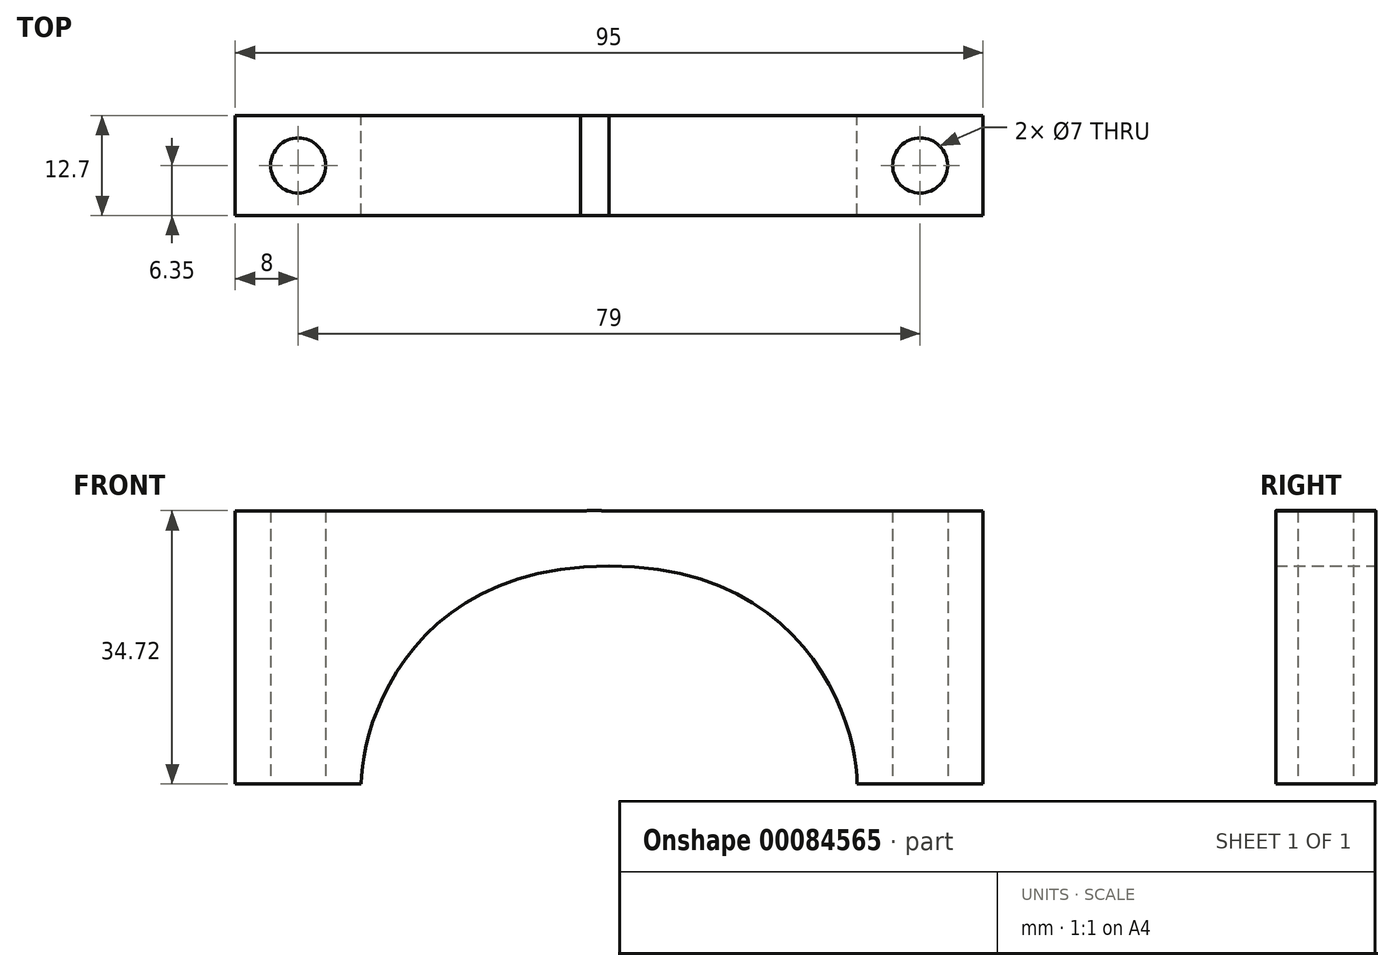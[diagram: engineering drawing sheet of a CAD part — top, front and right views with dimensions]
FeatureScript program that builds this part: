
annotation { "Feature Type Name" : "Feature", "Feature Type Description" : "" }
export const myFeature = defineFeature(function(context is Context, id is Id, definition is map)
    precondition{}
    {
        {
            var Q0;
            Q0=qCreatedBy(makeId("Front.planeOp"),FACE);
            var sketch = newSketch(context, id + "F0", { "sketchPlane" : qUnion([Q0]) });
            skPoint(sketch, "E0", {"position": v(0, 0) * mm});
            skPoint(sketch, "E1", {"position": v(0.85, 5.2) * mm});
            skPoint(sketch, "E2", {"position": v(3, 11.6) * mm});
            skPoint(sketch, "E3", {"position": v(6.2, 16.4) * mm});
            skPoint(sketch, "E4", {"position": v(11.3, 21) * mm});
            skPoint(sketch, "E5", {"position": v(15.8, 23.6) * mm});
            skPoint(sketch, "E6", {"position": v(22, 26.4) * mm});
            skPoint(sketch, "E7", {"position": v(31.5, 27.7) * mm});
            skFitSpline(sketch, "E8", {"points": [v(0, 0) * mm, v(31.5, 27.7) * mm], "startDerivative": vector(0, 22.39) * mm, "endDerivative": vector(76.41, 0) * mm});
            skLineSegment(sketch, "E9", {"start": v(31.5, 27.7) * mm, "end": v(0, 27.7) * mm, "construction": true});
            skLineSegment(sketch, "E10", {"start": v(0, 0) * mm, "end": v(-16, 0) * mm});
            skFitSpline(sketch, "E11.0", {"points": [v(-7, 0) * mm, v(-7, 0.7) * mm, v(-6.93, 2.14) * mm, v(-6.53, 5.25) * mm, v(-5.49, 9.57) * mm, v(-3.19, 15.24) * mm, v(0.43, 21.02) * mm, v(5.6, 26.46) * mm, v(12.5, 30.97) * mm, v(21.08, 33.97) * mm, v(27.85, 34.7) * mm, v(31.5, 34.7) * mm]});
            skLineSegment(sketch, "E12", {"start": v(-16, 0) * mm, "end": v(-16, 34.7) * mm});
            skLineSegment(sketch, "E13", {"start": v(-16, 34.7) * mm, "end": v(31.5, 34.7) * mm});
            skLineSegment(sketch, "E14", {"start": v(31.5, 34.7) * mm, "end": v(31.5, 27.7) * mm});
            skLineSegment(sketch, "E15.MirrorCS", {"start": v(79, 34.7) * mm, "end": v(31.5, 34.7) * mm});
            skFitSpline(sketch, "E16.MirrorCS", {"points": [v(63, 0) * mm, v(31.5, 27.7) * mm], "startDerivative": vector(0, 22.39) * mm, "endDerivative": vector(-76.41, 0) * mm});
            skLineSegment(sketch, "E17.MirrorCS", {"start": v(79, 0) * mm, "end": v(79, 34.7) * mm});
            skLineSegment(sketch, "E18.MirrorCS", {"start": v(63, 0) * mm, "end": v(79, 0) * mm});
            skSolve(sketch);
        }
        {
            var Q0;
            Q0 = qSketchRegion(id + "F0", true);
            extrude(context, id + "F1", {"entities" : qUnion([Q0]), "depth" : 12.7 * mm});
        }
        {
            var Q0;
            Q0=makeQuery(id+"F1.opExtrude","SWEPT_FACE",FACE,{"disambiguationData":[OSD([sQuery(id+"F0.wireOp",EDGE,"E10")])]});
            var sketch = newSketch(context, id + "F2", { "sketchPlane" : qUnion([Q0]) });
            skCircle(sketch, "E19", {"center": v(-8, 6.35) * mm, "radius": 3.5 * mm});
            skPoint(sketch, "E19.centerSnap0", {"position": v(-8, 12.7) * mm});
            skPoint(sketch, "E19.centerSnap1", {"position": v(-16, 6.35) * mm});
            skCircle(sketch, "E20.MirrorC", {"center": v(71, 6.35) * mm, "radius": 3.5 * mm});
            skSolve(sketch);
        }
        {
            var Q0;
            Q0 = qSketchRegion(id + "F2", true);
            extrude(context, id + "F3", {"entities" : qUnion([Q0]), "operationType" : NewBodyOperationType.REMOVE, "endBound" : BoundingType.THROUGH_ALL, "oppositeDirection" : true, "depth" : 25 * mm});
        }
    });
